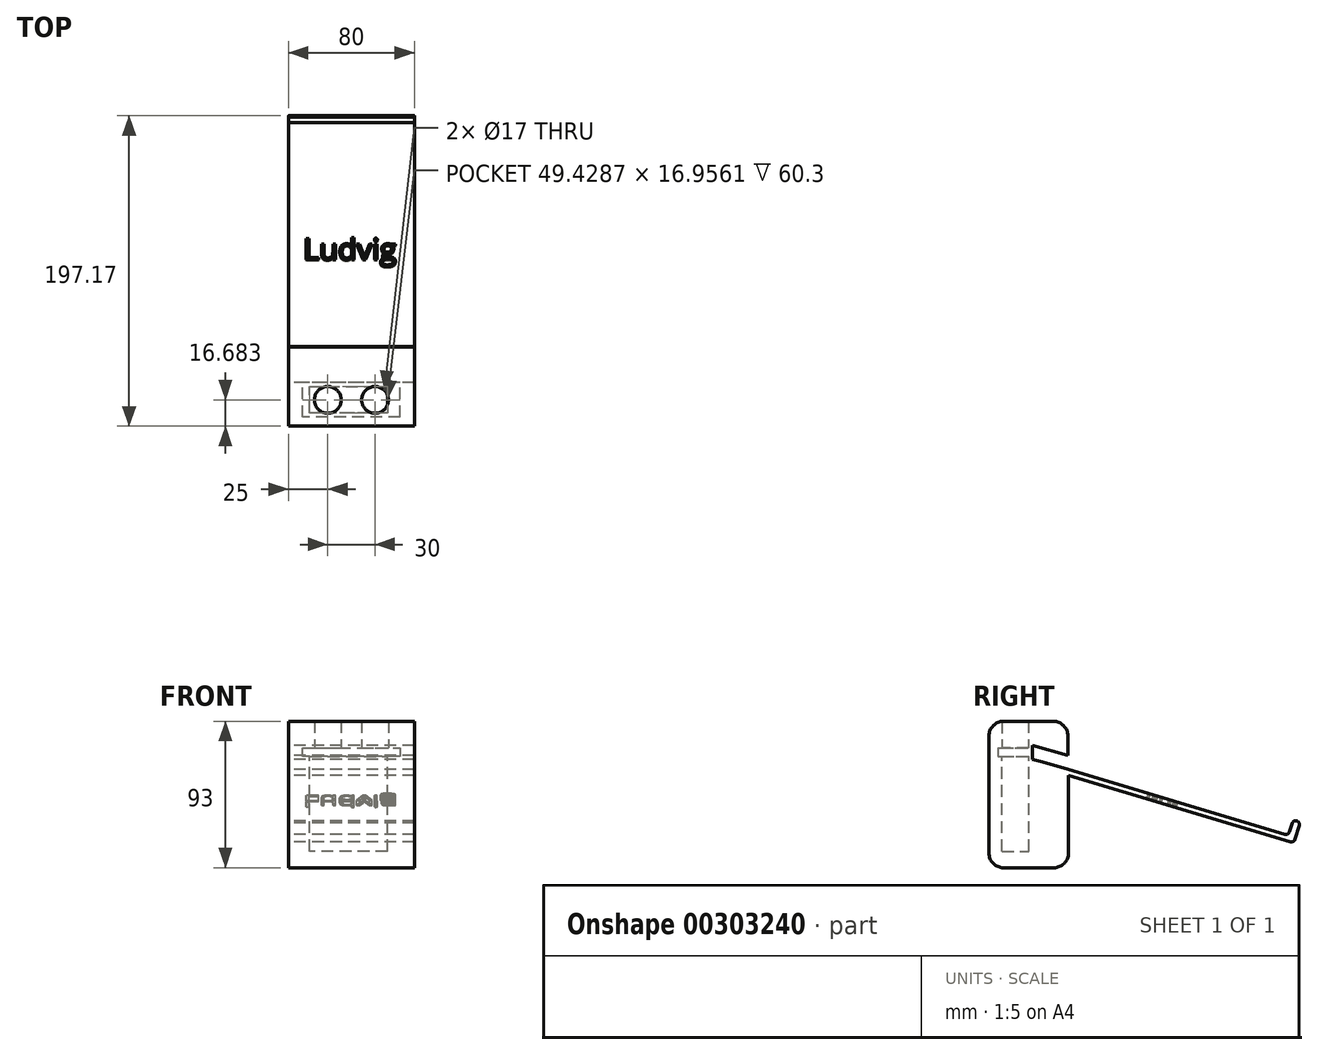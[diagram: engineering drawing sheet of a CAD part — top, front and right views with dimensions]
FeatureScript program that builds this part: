
annotation { "Feature Type Name" : "Feature", "Feature Type Description" : "" }
export const myFeature = defineFeature(function(context is Context, id is Id, definition is map)
    precondition{}
    {
        {
            var Q0;
            Q0=qCreatedBy(makeId("Right.planeOp"),FACE);
            var sketch = newSketch(context, id + "F0", { "sketchPlane" : qUnion([Q0])});
            skLineSegment(sketch, "E0.bottom", {"start": v(-41.55, 22.18) * mm, "end": v(-73.11, 22.18) * mm});
            skLineSegment(sketch, "E0.top", {"start": v(-41.22, -70.82) * mm, "end": v(-73.11, -70.82) * mm});
            skLineSegment(sketch, "E0.right", {"start": v(-82.43, 12.86) * mm, "end": v(-82.43, -61.5) * mm});
            skLineSegment(sketch, "E1", {"start": v(-31.87, -12.05) * mm, "end": v(109.12, -54.23) * mm});
            skLineSegment(sketch, "E2", {"start": v(112.04, -52.66) * mm, "end": v(114.63, -44) * mm});
            skLineSegment(sketch, "E3", {"start": v(105.57, -49.56) * mm, "end": v(-31.87, -8.44) * mm});
            skPoint(sketch, "E4.visualSharp", {"position": v(115.1, -42.44) * mm});
            skPoint(sketch, "E5.visualSharp", {"position": v(111.6, -39.48) * mm});
            skPoint(sketch, "E6.visualSharp", {"position": v(111.05, -51.2) * mm});
            skPoint(sketch, "E7.visualSharp", {"position": v(-32.23, -70.82) * mm});
            skArc(sketch, "E7.filletArc", {"start": v(-41.22, -70.82) * mm, "mid": v(-34.63, -68.1) * mm, "end": v(-31.9, -61.5) * mm});
            skPoint(sketch, "E8.visualSharp", {"position": v(-82.43, -70.82) * mm});
            skArc(sketch, "E8.filletArc", {"start": v(-82.43, -61.5) * mm, "mid": v(-79.7, -68.1) * mm, "end": v(-73.11, -70.82) * mm});
            skPoint(sketch, "E9.visualSharp", {"position": v(-82.43, 22.18) * mm});
            skArc(sketch, "E9.filletArc", {"start": v(-73.11, 22.18) * mm, "mid": v(-79.7, 19.45) * mm, "end": v(-82.43, 12.86) * mm});
            skPoint(sketch, "E10.visualSharp", {"position": v(-32.23, 22.18) * mm});
            skArc(sketch, "E10.filletArc", {"start": v(-32.23, 12.86) * mm, "mid": v(-34.96, 19.45) * mm, "end": v(-41.55, 22.18) * mm});
            skLineSegment(sketch, "E11", {"start": v(113.95, -41.48) * mm, "end": v(113.87, -41.4) * mm});
            skPoint(sketch, "E12.start.orphan", {"position": v(73.7, -32.59) * mm});
            skPoint(sketch, "E13.visualSharp", {"position": v(115.1, -42.45) * mm});
            skArc(sketch, "E13.filletArc", {"start": v(114.63, -44) * mm, "mid": v(114.64, -42.59) * mm, "end": v(113.87, -41.4) * mm});
            skPoint(sketch, "E14.visualSharp", {"position": v(109.72, -42.66) * mm});
            skArc(sketch, "E15.filletArc", {"start": v(113.95, -41.48) * mm, "mid": v(111.93, -40.97) * mm, "end": v(110.3, -42.26) * mm});
            skPoint(sketch, "E16.start.orphan", {"position": v(111.05, -40.66) * mm});
            skLineSegment(sketch, "E17", {"start": v(108.48, -48.01) * mm, "end": v(110.3, -42.26) * mm});
            skPoint(sketch, "E18.visualSharp", {"position": v(111.37, -54.9) * mm});
            skArc(sketch, "E18.filletArc", {"start": v(109.12, -54.23) * mm, "mid": v(110.9, -54.05) * mm, "end": v(112.04, -52.66) * mm});
            skPoint(sketch, "E19.visualSharp", {"position": v(107.79, -50.22) * mm});
            skArc(sketch, "E19.filletArc", {"start": v(105.57, -49.56) * mm, "mid": v(107.34, -49.38) * mm, "end": v(108.48, -48.01) * mm});
            skPoint(sketch, "E20.start.orphan", {"position": v(-39.95, -9.64) * mm});
            skPoint(sketch, "E21.end.orphan", {"position": v(-39.95, -6.02) * mm});
            skPoint(sketch, "E22.end.orphan", {"position": v(-39.95, 1.43) * mm});
            skLineSegment(sketch, "E23.trimOffspring", {"start": v(-31.87, -12.05) * mm, "end": v(-31.9, -61.5) * mm});
            skPoint(sketch, "E24.end.orphan", {"position": v(-39.95, 8.1) * mm});
            skLineSegment(sketch, "E25", {"start": v(-32.23, 12.86) * mm, "end": v(-32.23, 0.5) * mm});
            skLineSegment(sketch, "E26", {"start": v(-32.23, 0.5) * mm, "end": v(-50.43, 5.7) * mm});
            skLineSegment(sketch, "E27", {"start": v(-31.87, -8.44) * mm, "end": v(-50.4, -3.15) * mm});
            skLineSegment(sketch, "E28", {"start": v(-50.43, 0) * mm, "end": v(-50.43, 0) * mm});
            skPoint(sketch, "E29.trimOffspring.end.orphan", {"position": v(-50.43, -6.62) * mm});
            skLineSegment(sketch, "E30.trimOffspring", {"start": v(-50.4, -0.8) * mm, "end": v(-50.4, -0.8) * mm});
            skLineSegment(sketch, "E31", {"start": v(-78.04, 0.9) * mm, "end": v(-78.04, -69.41) * mm});
            skLineSegment(sketch, "E32", {"start": v(-75, -6.36) * mm, "end": v(-75, -70.63) * mm});
            skLineSegment(sketch, "E33", {"start": v(-78.04, 0.9) * mm, "end": v(-78.04, -1.9) * mm});
            skPoint(sketch, "E34.orphan", {"position": v(-75, -0.9) * mm});
            skPoint(sketch, "E35.visualSharp", {"position": v(-78.04, 2.49) * mm});
            skArc(sketch, "E35.filletArc", {"start": v(-73.65, 2.49) * mm, "mid": v(-76.75, 1.2) * mm, "end": v(-78.04, -1.9) * mm});
            skPoint(sketch, "E36.visualSharp", {"position": v(-75, -1.97) * mm});
            skArc(sketch, "E36.filletArc", {"start": v(-70.62, -1.97) * mm, "mid": v(-73.72, -3.26) * mm, "end": v(-75, -6.36) * mm});
            skLineSegment(sketch, "E37", {"start": v(-46.5, 4.58) * mm, "end": v(-54.75, 6.93) * mm});
            skLineSegment(sketch, "E38", {"start": v(-54.75, 6.93) * mm, "end": v(-54.75, -1.91) * mm});
            skLineSegment(sketch, "E39", {"start": v(-54.75, -1.91) * mm, "end": v(-48.5, -3.7) * mm});
            skLineSegment(sketch, "E40", {"start": v(-48.5, -3.7) * mm, "end": v(-36.3, -7.17) * mm});
            skSolve(sketch);
        }
        {
            var Q0;
            Q0 = qSketchRegion(id + "F0", true);
            extrude(context, id + "F1", {"entities" : qUnion([Q0]), "depth" : 80 * mm});
        }
        {
            var Q0;
            Q0=makeQuery(id+"F1.opExtrude","SWEPT_FACE",FACE,{"disambiguationData":[OSD([sQuery(id+"F0.wireOp",EDGE,"E3")])]});
            var sketch = newSketch(context, id + "F2", { "sketchPlane" : qUnion([Q0])});
            skSolve(sketch);
        }
        {
            var Q0;
            Q0=makeQuery(id+"F1.opExtrude","SWEPT_FACE",FACE,{"disambiguationData":[OSD([sQuery(id+"F0.wireOp",EDGE,"E38")])]});
            var sketch = newSketch(context, id + "F3", { "sketchPlane" : qUnion([Q0])});
            skLineSegment(sketch, "E41", {"start": v(-71, 2.5) * mm, "end": v(-71, 0) * mm});
            skPoint(sketch, "E41.startSnap0", {"position": v(-80, 2.5) * mm});
            skLineSegment(sketch, "E42", {"start": v(-71, 0) * mm, "end": v(-9, 0) * mm});
            skLineSegment(sketch, "E43", {"start": v(-9, 0) * mm, "end": v(-9, 5.19) * mm});
            skLineSegment(sketch, "E44", {"start": v(-9, 5.19) * mm, "end": v(-69.08, 5.19) * mm});
            skLineSegment(sketch, "E45", {"start": v(-69.08, 5.19) * mm, "end": v(-71, 5.19) * mm});
            skLineSegment(sketch, "E46", {"start": v(-71, 5.19) * mm, "end": v(-71, 0) * mm});
            skSolve(sketch);
        }
        {
            var Q0;
            Q0 = qSketchRegion(id + "F3", true);
            extrude(context, id + "F4", {"entities" : qUnion([Q0]), "operationType" : NewBodyOperationType.REMOVE, "oppositeDirection" : true, "depth" : 22 * mm});
        }
        {
            var Q0;
            Q0=makeQuery(id+"F4.boolean.opBoolean","COPY",FACE,{"derivedFrom":makeQuery(id+"F4.opExtrude","SWEPT_FACE",FACE,{"disambiguationData":[OSD([sQuery(id+"F3.wireOp",EDGE,"E44"),sQuery(id+"F3.wireOp",EDGE,"E45")])]})});
            var sketch = newSketch(context, id + "F5", { "sketchPlane" : qUnion([Q0])});
            skCircle(sketch, "E47", {"center": v(55, 65.75) * mm, "radius": 8.5 * mm});
            skPoint(sketch, "E47.centerSnap0", {"position": v(71, 65.75) * mm});
            skCircle(sketch, "E48", {"center": v(25, 65.75) * mm, "radius": 8.5 * mm});
            skSolve(sketch);
        }
        {
            var Q0;
            Q0 = qSketchRegion(id + "F5", true);
            extrude(context, id + "F6", {"entities" : qUnion([Q0]), "operationType" : NewBodyOperationType.REMOVE, "oppositeDirection" : true, "depth" : 22.5 * mm});
        }
        {
            var Q0;
            Q0=makeQuery(id+"F4.boolean.opBoolean","COPY",FACE,{"derivedFrom":makeQuery(id+"F4.opExtrude","SWEPT_FACE",FACE,{"disambiguationData":[OSD([sQuery(id+"F3.wireOp",EDGE,"E42")])]})});
            var sketch = newSketch(context, id + "F7", { "sketchPlane" : qUnion([Q0])});
            skLineSegment(sketch, "E49", {"start": v(13.5, -74.1) * mm, "end": v(13.5, -57.14) * mm});
            skLineSegment(sketch, "E50", {"start": v(13.5, -57.14) * mm, "end": v(62.94, -57.14) * mm});
            skLineSegment(sketch, "E51", {"start": v(62.94, -57.14) * mm, "end": v(62.94, -74.1) * mm});
            skLineSegment(sketch, "E52", {"start": v(62.94, -74.1) * mm, "end": v(13.5, -74.1) * mm});
            skSolve(sketch);
        }
        {
            var Q0;
            Q0 = qSketchRegion(id + "F7", true);
            extrude(context, id + "F8", {"entities" : qUnion([Q0]), "operationType" : NewBodyOperationType.REMOVE, "oppositeDirection" : true, "depth" : 60.3 * mm});
        }
        {
            var Q0;
            {var subQ0=sQuery(id+"F0.wireOp",EDGE,"E3");Q0=makeQuery(id+"F2.imprint","IMPRINT",FACE,{"disambiguationData":[TD([[makeQuery(id+"F2.imprint","IMPRINT",EDGE,{"derivedFrom":makeQuery(id+"F1.opExtrude","CAP_EDGE",EDGE,{"disambiguationData":[OSD([subQ0])],"isStart":true})}),1.0]])]});}
            var sketch = newSketch(context, id + "F9", { "sketchPlane" : qUnion([Q0])});
            skText(sketch, "E53", { "text": "Ludvig", "fontName": "OpenSans-Regular.ttf"});
            skLineSegment(sketch, "E54", {"start": v(58.49, 28.33) * mm, "end": v(68, 28.33) * mm});
            skLineSegment(sketch, "E55", {"start": v(68, 28.33) * mm, "end": v(68.04, 28.33) * mm});
            skLineSegment(sketch, "E56", {"start": v(68.04, 28.33) * mm, "end": v(68.04, 28.29) * mm});
            skLineSegment(sketch, "E57", {"start": v(68.04, 28.29) * mm, "end": v(68.04, 28.16) * mm});
            skLineSegment(sketch, "E58", {"start": v(68.04, 28.16) * mm, "end": v(68.03, 28.13) * mm});
            skLineSegment(sketch, "E59", {"start": v(68.03, 28.13) * mm, "end": v(58.49, 28.16) * mm});
            skLineSegment(sketch, "E60", {"start": v(58.49, 28.16) * mm, "end": v(58.4, 28.16) * mm});
            skLineSegment(sketch, "E61", {"start": v(58.4, 28.16) * mm, "end": v(58.4, 28.18) * mm});
            skLineSegment(sketch, "E62", {"start": v(58.4, 28.18) * mm, "end": v(58.42, 28.27) * mm});
            skLineSegment(sketch, "E63", {"start": v(58.42, 28.27) * mm, "end": v(58.43, 28.33) * mm});
            skLineSegment(sketch, "E64", {"start": v(58.43, 28.33) * mm, "end": v(58.49, 28.33) * mm});
            const initialGuessF9  = {"E53": [0.00944, 0.02953, 1, 0, 0.01399]};
            skSetInitialGuess(sketch, initialGuessF9);
            skSolve(sketch);
        }
        {
            var Q0;
            Q0 = qSketchRegion(id + "F9", true);
            extrude(context, id + "F10", {"entities" : qUnion([Q0]), "operationType" : NewBodyOperationType.REMOVE, "oppositeDirection" : true, "depth" : 25 * mm});
        }
    });
